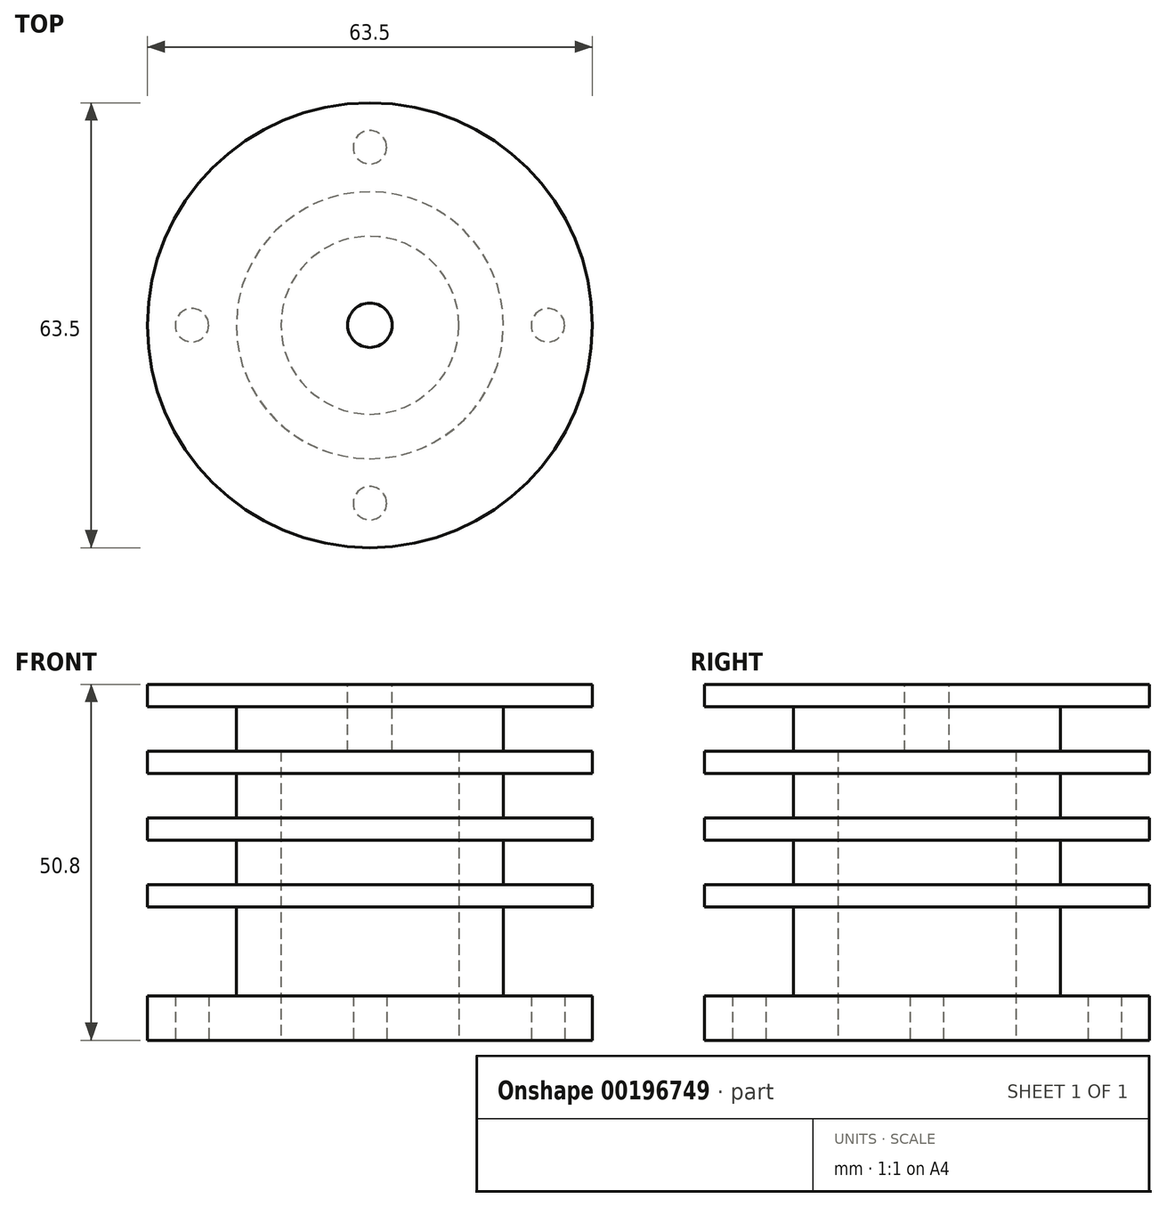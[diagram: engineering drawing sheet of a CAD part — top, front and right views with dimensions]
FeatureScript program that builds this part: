
annotation { "Feature Type Name" : "Feature", "Feature Type Description" : "" }
export const myFeature = defineFeature(function(context is Context, id is Id, definition is map)
    precondition{}
    {
        {
            var Q0;
            Q0=qCreatedBy(makeId("Top.planeOp"),FACE);
            var sketch = newSketch(context, id + "F0", { "sketchPlane" : qUnion([Q0])});
            skCircle(sketch, "E0", {"center": v(0, 0) * mm, "radius": 19.05 * mm});
            skSolve(sketch);
        }
        {
            var Q0;
            Q0=makeQuery(id+"F0.imprint","IMPRINT",FACE,{"disambiguationData":[TD([[makeQuery(id+"F0.imprint","IMPRINT",EDGE,{"derivedFrom":sQuery(id+"F0.wireOp",EDGE,"E0")}),1.0]])]});
            extrude(context, id + "F1", {"entities" : qUnion([Q0]), "depth" : 25.4 * mm, "hasSecondDirection" : true, "secondDirectionOppositeDirection" : true, "secondDirectionDepth" : 25.4 * mm});
        }
        {
            var Q0;
            Q0=makeQuery(id+"F1.opExtrude","CAP_FACE",FACE,{"disambiguationData":[OSD([sQuery(id+"F0.wireOp",EDGE,"E0"),sQuery(id+"F0.wireOp",EDGE,"NknTRvBC-EepX-mJMP-RdsP-QHHfBHyxjFbN")])],"isStart":true});
            var sketch = newSketch(context, id + "F2", { "sketchPlane" : qUnion([Q0])});
            skCircle(sketch, "E1", {"center": v(0, 0) * mm, "radius": 31.75 * mm});
            skCircle(sketch, "E2", {"center": v(0, 25.4) * mm, "radius": 2.38 * mm});
            skCircle(sketch, "E3", {"center": v(25.4, 0) * mm, "radius": 2.38 * mm});
            skCircle(sketch, "E4", {"center": v(0, -25.4) * mm, "radius": 2.38 * mm});
            skCircle(sketch, "E5", {"center": v(-25.4, 0) * mm, "radius": 2.38 * mm});
            skSolve(sketch);
        }
        {
            var Q0;
            Q0=makeQuery(id+"F2.imprint","IMPRINT",FACE,{"disambiguationData":[TD([[makeQuery(id+"F2.imprint","IMPRINT",EDGE,{"derivedFrom":sQuery(id+"F2.wireOp",EDGE,"E1")}),1.0]])]});
            extrude(context, id + "F3", {"entities" : qUnion([Q0]), "operationType" : NewBodyOperationType.ADD, "oppositeDirection" : true, "depth" : 6.35 * mm});
        }
        {
            var Q0;
            {var subQ0=sQuery(id+"F0.wireOp",EDGE,"E0");Q0=makeQuery(id+"F3.boolean.opBoolean","MERGE",FACE,{"derivedFrom":[makeQuery(id+"F1.opExtrude","CAP_FACE",FACE,{"disambiguationData":[OSD([subQ0])],"isStart":true}),makeQuery(id+"F3.opExtrude","CAP_FACE",FACE,{"disambiguationData":[OSD([subQ0,sQuery(id+"F2.wireOp",EDGE,"E1"),sQuery(id+"F2.wireOp",EDGE,"E2"),sQuery(id+"F2.wireOp",EDGE,"E3"),sQuery(id+"F2.wireOp",EDGE,"E4"),sQuery(id+"F2.wireOp",EDGE,"E5")])],"isStart":true})]});}
            var sketch = newSketch(context, id + "F4", { "sketchPlane" : qUnion([Q0])});
            skCircle(sketch, "E6", {"center": v(0, 0) * mm, "radius": 12.7 * mm});
            skSolve(sketch);
        }
        {
            var Q0;
            Q0=makeQuery(id+"F4.imprint","IMPRINT",FACE,{"disambiguationData":[TD([[makeQuery(id+"F4.imprint","IMPRINT",EDGE,{"derivedFrom":sQuery(id+"F4.wireOp",EDGE,"E6")}),1.0]])]});
            extrude(context, id + "F5", {"entities" : qUnion([Q0]), "operationType" : NewBodyOperationType.REMOVE, "oppositeDirection" : true, "depth" : 41.27 * mm});
        }
        {
            var Q0;
            Q0=makeQuery(id+"F1.opExtrude","CAP_FACE",FACE,{"disambiguationData":[OSD([sQuery(id+"F0.wireOp",EDGE,"E0")])],"isStart":false});
            var sketch = newSketch(context, id + "F6", { "sketchPlane" : qUnion([Q0])});
            skCircle(sketch, "E7", {"center": v(0, 0) * mm, "radius": 3.18 * mm});
            skSolve(sketch);
        }
        {
            var Q0;
            Q0=makeQuery(id+"F6.imprint","IMPRINT",FACE,{"disambiguationData":[TD([[makeQuery(id+"F6.imprint","IMPRINT",EDGE,{"derivedFrom":sQuery(id+"F6.wireOp",EDGE,"E7")}),1.0]])]});
            extrude(context, id + "F7", {"entities" : qUnion([Q0]), "operationType" : NewBodyOperationType.REMOVE, "oppositeDirection" : true, "depth" : 9.52 * mm});
        }
        {
            var Q0;
            Q0=makeQuery(id+"F1.opExtrude","CAP_FACE",FACE,{"disambiguationData":[OSD([sQuery(id+"F0.wireOp",EDGE,"E0")])],"isStart":false});
            var sketch = newSketch(context, id + "F8", { "sketchPlane" : qUnion([Q0])});
            skCircle(sketch, "E8", {"center": v(0, 0) * mm, "radius": 31.75 * mm});
            skSolve(sketch);
        }
        {
            var Q0;
            Q0=makeQuery(id+"F8.imprint","IMPRINT",FACE,{"disambiguationData":[TD([[makeQuery(id+"F8.imprint","IMPRINT",EDGE,{"derivedFrom":sQuery(id+"F8.wireOp",EDGE,"E8")}),1.0]])]});
            extrude(context, id + "F9", {"entities" : qUnion([Q0]), "operationType" : NewBodyOperationType.ADD, "oppositeDirection" : true, "depth" : 3.17 * mm});
        }
        {
            var Q0;
            Q0=makeQuery(id+"F9.opExtrude","CAP_FACE",FACE,{"disambiguationData":[OSD([sQuery(id+"F0.wireOp",EDGE,"E0"),sQuery(id+"F8.wireOp",EDGE,"E8")])],"isStart":false});
            cPlane(context, id + "F10", {"entities" : qUnion([Q0]), "cplaneType" : CPlaneType.OFFSET, "offset" : 6.35 * mm, "width" : 152.4 * mm, "height" : 152.4 * mm});
        }
        {
            var Q0;
            Q0=makeQuery(id+"F9.opExtrude","CAP_FACE",FACE,{"disambiguationData":[OSD([sQuery(id+"F0.wireOp",EDGE,"E0"),sQuery(id+"F8.wireOp",EDGE,"E8")])],"isStart":false});
            cPlane(context, id + "F11", {"entities" : qUnion([Q0]), "cplaneType" : CPlaneType.OFFSET, "offset" : 15.88 * mm, "width" : 152.4 * mm, "height" : 152.4 * mm});
        }
        {
            var Q0;
            Q0=makeQuery(id+"F9.opExtrude","CAP_FACE",FACE,{"disambiguationData":[OSD([sQuery(id+"F0.wireOp",EDGE,"E0"),sQuery(id+"F8.wireOp",EDGE,"E8")])],"isStart":false});
            cPlane(context, id + "F12", {"entities" : qUnion([Q0]), "cplaneType" : CPlaneType.OFFSET, "offset" : 25.4 * mm, "width" : 152.4 * mm, "height" : 152.4 * mm});
        }
        {
            var Q0;
            Q0=qCreatedBy(id+"F10.planeOp",FACE);
            var sketch = newSketch(context, id + "F13", { "sketchPlane" : qUnion([Q0])});
            skCircle(sketch, "E9", {"center": v(0, 0) * mm, "radius": 31.75 * mm});
            skCircle(sketch, "E10", {"center": v(0, 0) * mm, "radius": 12.7 * mm});
            skSolve(sketch);
        }
        {
            var Q0;
            Q0=makeQuery(id+"F13.imprint","IMPRINT",FACE,{"disambiguationData":[TD([[makeQuery(id+"F13.imprint","IMPRINT",EDGE,{"derivedFrom":sQuery(id+"F13.wireOp",EDGE,"E9")}),1.0]])]});
            extrude(context, id + "F14", {"entities" : qUnion([Q0]), "operationType" : NewBodyOperationType.ADD, "depth" : 3.17 * mm});
        }
        {
            var Q0;
            Q0=qCreatedBy(id+"F11.planeOp",FACE);
            var sketch = newSketch(context, id + "F15", { "sketchPlane" : qUnion([Q0])});
            skCircle(sketch, "E11", {"center": v(0, 0) * mm, "radius": 31.75 * mm});
            skCircle(sketch, "E12", {"center": v(0, 0) * mm, "radius": 12.7 * mm});
            skSolve(sketch);
        }
        {
            var Q0;
            Q0=makeQuery(id+"F15.imprint","IMPRINT",FACE,{"disambiguationData":[TD([[makeQuery(id+"F15.imprint","IMPRINT",EDGE,{"derivedFrom":sQuery(id+"F15.wireOp",EDGE,"E11")}),1.0]])]});
            extrude(context, id + "F16", {"entities" : qUnion([Q0]), "operationType" : NewBodyOperationType.ADD, "depth" : 3.17 * mm});
        }
        {
            var Q0;
            Q0=qCreatedBy(id+"F12.planeOp",FACE);
            var sketch = newSketch(context, id + "F17", { "sketchPlane" : qUnion([Q0])});
            skCircle(sketch, "E13", {"center": v(0, 0) * mm, "radius": 31.75 * mm});
            skCircle(sketch, "E14", {"center": v(0, 0) * mm, "radius": 12.7 * mm});
            skSolve(sketch);
        }
        {
            var Q0;
            Q0=makeQuery(id+"F17.imprint","IMPRINT",FACE,{"disambiguationData":[TD([[makeQuery(id+"F17.imprint","IMPRINT",EDGE,{"derivedFrom":sQuery(id+"F17.wireOp",EDGE,"E13")}),1.0]])]});
            extrude(context, id + "F18", {"entities" : qUnion([Q0]), "operationType" : NewBodyOperationType.ADD, "depth" : 3.17 * mm});
        }
    });
